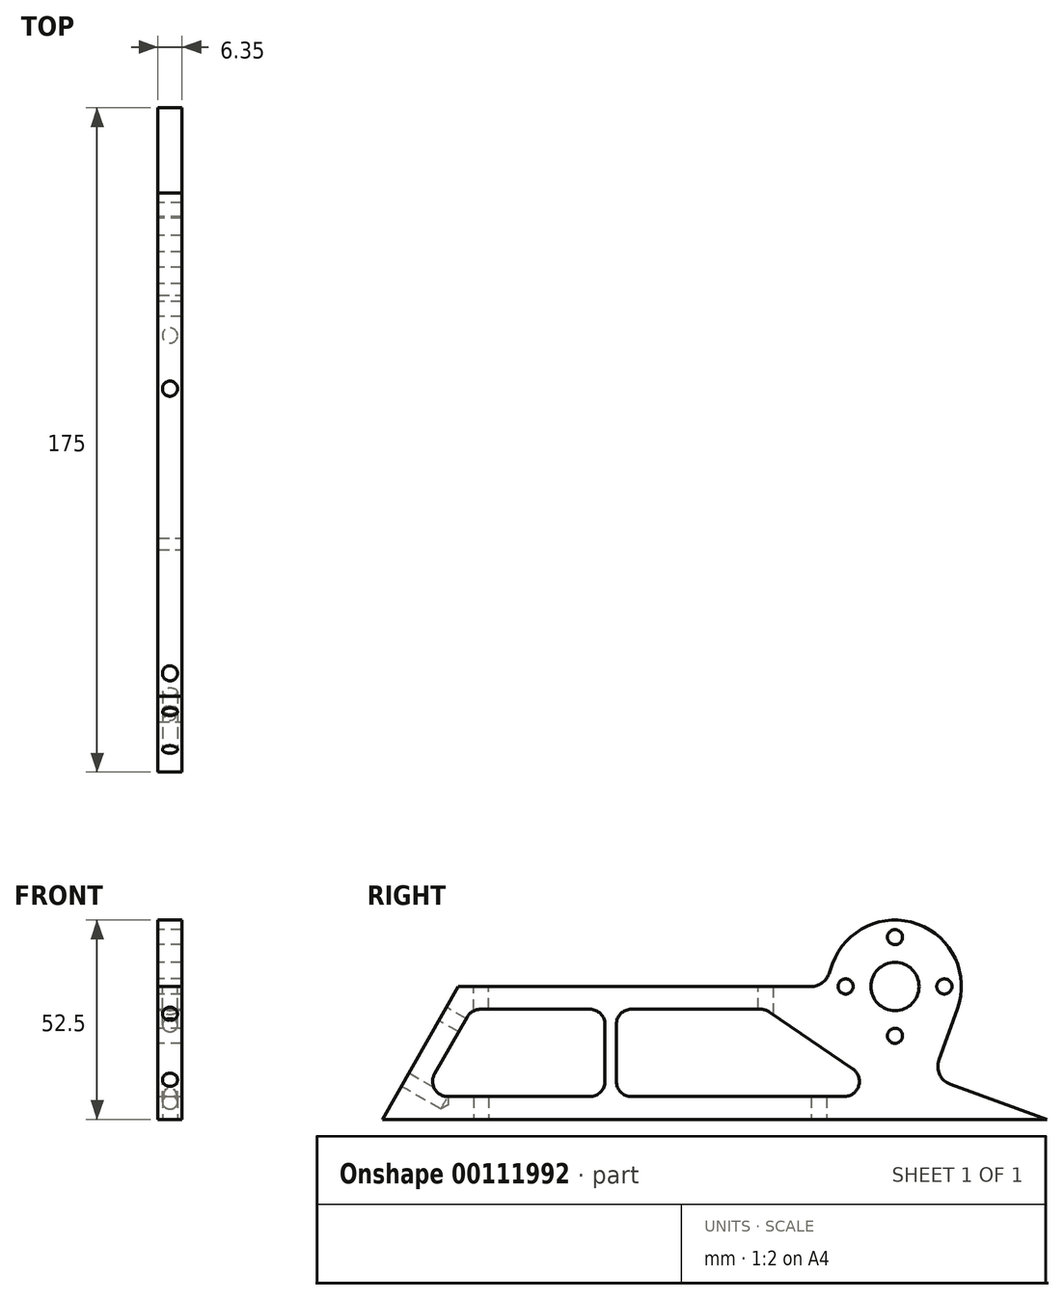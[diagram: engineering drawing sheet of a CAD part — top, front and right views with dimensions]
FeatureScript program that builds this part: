
annotation { "Feature Type Name" : "Feature", "Feature Type Description" : "" }
export const myFeature = defineFeature(function(context is Context, id is Id, definition is map)
    precondition{}
    {
        {
            var Q0;
            Q0=qCreatedBy(makeId("Right.planeOp"),FACE);
            var sketch = newSketch(context, id + "F0", { "sketchPlane" : qUnion([Q0])});
            skLineSegment(sketch, "E0", {"start": v(0, 0) * mm, "end": v(-30.13, 10.96) * mm});
            skLineSegment(sketch, "E1", {"start": v(-58.62, 35) * mm, "end": v(-155, 35) * mm});
            skLineSegment(sketch, "E2", {"start": v(-155, 35) * mm, "end": v(-175, 0) * mm});
            skLineSegment(sketch, "E3", {"start": v(-175, 0) * mm, "end": v(0, 0) * mm});
            skCircle(sketch, "E4", {"center": v(-88.38, 18) * mm, "radius": 14 * mm, "construction": true});
            skCircle(sketch, "E5", {"center": v(-40, 35) * mm, "radius": 34.3 * mm, "construction": true});
            skCircle(sketch, "E6", {"center": v(-130, 17.5) * mm, "radius": 11 * mm, "construction": true});
            skCircle(sketch, "E7", {"center": v(-40, 35) * mm, "radius": 6.35 * mm});
            skCircle(sketch, "E8", {"center": v(-40, 35) * mm, "radius": 13 * mm, "construction": true});
            skCircle(sketch, "E9", {"center": v(-40, 48) * mm, "radius": 2 * mm});
            skCircle(sketch, "E10", {"center": v(-53, 35) * mm, "radius": 2 * mm});
            skCircle(sketch, "E11", {"center": v(-27, 35) * mm, "radius": 2 * mm});
            skCircle(sketch, "E12", {"center": v(-40, 22) * mm, "radius": 2 * mm});
            skCircle(sketch, "E13", {"center": v(-130, 17.5) * mm, "radius": 25.4 * mm, "construction": true});
            skLineSegment(sketch, "E14", {"start": v(-130, 17.5) * mm, "end": v(-130, 35) * mm, "construction": true});
            skLineSegment(sketch, "E15", {"start": v(-130, 17.5) * mm, "end": v(-130, 0) * mm, "construction": true});
            skLineSegment(sketch, "E16", {"start": v(-58.62, 35) * mm, "end": v(-56.44, 40.99) * mm});
            skArc(sketch, "E17", {"start": v(-23.56, 29.01) * mm, "mid": v(-34.01, 51.44) * mm, "end": v(-56.44, 40.99) * mm});
            skLineSegment(sketch, "E18", {"start": v(-23.56, 29.01) * mm, "end": v(-30.13, 10.96) * mm});
            skPoint(sketch, "E19.orphan", {"position": v(-90, 35) * mm});
            skCircle(sketch, "E20", {"center": v(-130, 17.5) * mm, "radius": 2 * mm});
            skCircle(sketch, "E21", {"center": v(-88.38, 18) * mm, "radius": 3 * mm});
            skSolve(sketch);
        }
        {
            var Q0;
            Q0=qSketchRegion(id+"F0",true);
            extrude(context, id + "F1", {"entities" : qUnion([Q0]), "depth" : 6.35 * mm});
        }
        {
            var Q0;
            Q0=makeQuery(id+"F1.opExtrude","SWEPT_EDGE",EDGE,{"disambiguationData":[OSD([sQuery(id+"F0.wireOp",EDGE,"E1"),sQuery(id+"F0.wireOp",EDGE,"E16")])]});
            var Q1;
            Q1=makeQuery(id+"F1.opExtrude","SWEPT_EDGE",EDGE,{"disambiguationData":[OSD([sQuery(id+"F0.wireOp",EDGE,"E0"),sQuery(id+"F0.wireOp",EDGE,"E18")])]});
            fillet(context, id + "F2", {"entities" : qUnion([Q0, Q1]), "radius" : 5 * mm, "tangentPropagation" : true, "allowEdgeOverflow" : false});
        }
        {
            var Q0;
            Q0=makeQuery(id+"F1.opExtrude","CAP_FACE",FACE,{"disambiguationData":[OSD([sQuery(id+"F0.wireOp",EDGE,"E0"),sQuery(id+"F0.wireOp",EDGE,"E1"),sQuery(id+"F0.wireOp",EDGE,"E2"),sQuery(id+"F0.wireOp",EDGE,"E3"),sQuery(id+"F0.wireOp",EDGE,"E7"),sQuery(id+"F0.wireOp",EDGE,"E9"),sQuery(id+"F0.wireOp",EDGE,"E10"),sQuery(id+"F0.wireOp",EDGE,"E11"),sQuery(id+"F0.wireOp",EDGE,"E12"),sQuery(id+"F0.wireOp",EDGE,"E16"),sQuery(id+"F0.wireOp",EDGE,"E17"),sQuery(id+"F0.wireOp",EDGE,"E18"),sQuery(id+"F0.wireOp",EDGE,"E20"),sQuery(id+"F0.wireOp",EDGE,"E21")])],"isStart":false});
            var sketch = newSketch(context, id + "F3", { "sketchPlane" : qUnion([Q0])});
            skPoint(sketch, "E22", {"position": v(-130, 17.5) * mm});
            skLineSegment(sketch, "E23", {"start": v(-79.38, 25) * mm, "end": v(-79.38, 10) * mm});
            skLineSegment(sketch, "E24", {"start": v(-75.38, 6) * mm, "end": v(-53.38, 6) * mm});
            skLineSegment(sketch, "E25", {"start": v(-51.13, 13.3) * mm, "end": v(-73.13, 28.3) * mm});
            skPoint(sketch, "E26.visualSharp", {"position": v(-79.38, 32.57) * mm});
            skArc(sketch, "E26.filletArc", {"start": v(-73.13, 28.3) * mm, "mid": v(-77.25, 28.54) * mm, "end": v(-79.38, 25) * mm});
            skPoint(sketch, "E27.visualSharp", {"position": v(-40.41, 6) * mm});
            skArc(sketch, "E27.filletArc", {"start": v(-53.38, 6) * mm, "mid": v(-49.56, 8.82) * mm, "end": v(-51.13, 13.3) * mm});
            skPoint(sketch, "E28.visualSharp", {"position": v(-79.38, 6) * mm});
            skArc(sketch, "E28.filletArc", {"start": v(-79.38, 10) * mm, "mid": v(-78.2, 7.17) * mm, "end": v(-75.38, 6) * mm});
            skSolve(sketch);
        }
        {
            var Q0;
            Q0=qSketchRegion(id+"F3",true);
            extrude(context, id + "F4", {"entities" : qUnion([Q0]), "operationType" : NewBodyOperationType.REMOVE, "endBound" : BoundingType.THROUGH_ALL, "oppositeDirection" : true, "depth" : 25 * mm});
        }
        {
            var Q0;
            Q0=makeQuery(id+"F1.opExtrude","CAP_FACE",FACE,{"disambiguationData":[OSD([sQuery(id+"F0.wireOp",EDGE,"E0"),sQuery(id+"F0.wireOp",EDGE,"E1"),sQuery(id+"F0.wireOp",EDGE,"E2"),sQuery(id+"F0.wireOp",EDGE,"E3"),sQuery(id+"F0.wireOp",EDGE,"E7"),sQuery(id+"F0.wireOp",EDGE,"E9"),sQuery(id+"F0.wireOp",EDGE,"E10"),sQuery(id+"F0.wireOp",EDGE,"E11"),sQuery(id+"F0.wireOp",EDGE,"E12"),sQuery(id+"F0.wireOp",EDGE,"E16"),sQuery(id+"F0.wireOp",EDGE,"E17"),sQuery(id+"F0.wireOp",EDGE,"E18"),sQuery(id+"F0.wireOp",EDGE,"E20"),sQuery(id+"F0.wireOp",EDGE,"E21")])],"isStart":false});
            var sketch = newSketch(context, id + "F5", { "sketchPlane" : qUnion([Q0])});
            skLineSegment(sketch, "E29.bottom", {"start": v(-113.38, 29) * mm, "end": v(-75.38, 29) * mm});
            skLineSegment(sketch, "E29.top", {"start": v(-113.38, 6) * mm, "end": v(-75.38, 6) * mm});
            skLineSegment(sketch, "E29.left", {"start": v(-113.38, 29) * mm, "end": v(-113.38, 6) * mm});
            skLineSegment(sketch, "E29.right", {"start": v(-75.38, 29) * mm, "end": v(-75.38, 6) * mm});
            skLineSegment(sketch, "E30.bottom", {"start": v(-116.38, 29) * mm, "end": v(-151.52, 29) * mm});
            skLineSegment(sketch, "E30.top", {"start": v(-116.38, 6) * mm, "end": v(-164.66, 6) * mm});
            skLineSegment(sketch, "E30.left", {"start": v(-116.38, 29) * mm, "end": v(-116.38, 6) * mm});
            skLineSegment(sketch, "E30.right", {"start": v(-151.52, 29) * mm, "end": v(-164.66, 6) * mm});
            skPoint(sketch, "E31", {"position": v(-40, 35) * mm});
            skSolve(sketch);
        }
        {
            var Q0;
            Q0=qSketchRegion(id+"F5",true);
            extrude(context, id + "F6", {"entities" : qUnion([Q0]), "operationType" : NewBodyOperationType.REMOVE, "endBound" : BoundingType.THROUGH_ALL, "oppositeDirection" : true, "depth" : 25 * mm});
        }
        {
            var Q0;
            Q0=makeQuery(id+"F6.boolean.opBoolean","COPY",EDGE,{"derivedFrom":makeQuery(id+"F6.opExtrude","SWEPT_EDGE",EDGE,{"disambiguationData":[OSD([sQuery(id+"F5.wireOp",EDGE,"E30.bottom"),sQuery(id+"F5.wireOp",EDGE,"E30.left")])]})});
            var Q1;
            Q1=makeQuery(id+"F6.boolean.opBoolean","COPY",EDGE,{"derivedFrom":makeQuery(id+"F6.opExtrude","SWEPT_EDGE",EDGE,{"disambiguationData":[OSD([sQuery(id+"F5.wireOp",EDGE,"E29.bottom"),sQuery(id+"F5.wireOp",EDGE,"E29.right")])]})});
            var Q2;
            Q2=makeQuery(id+"F6.boolean.opBoolean","COPY",EDGE,{"derivedFrom":makeQuery(id+"F6.opExtrude","SWEPT_EDGE",EDGE,{"disambiguationData":[OSD([sQuery(id+"F5.wireOp",EDGE,"E30.top"),sQuery(id+"F5.wireOp",EDGE,"E30.left")])]})});
            var Q3;
            Q3=makeQuery(id+"F6.boolean.opBoolean","COPY",EDGE,{"derivedFrom":makeQuery(id+"F6.opExtrude","SWEPT_EDGE",EDGE,{"disambiguationData":[OSD([sQuery(id+"F5.wireOp",EDGE,"E29.top"),sQuery(id+"F5.wireOp",EDGE,"E29.right")])]})});
            var Q4;
            Q4=makeQuery(id+"F6.boolean.opBoolean","COPY",EDGE,{"derivedFrom":makeQuery(id+"F6.opExtrude","SWEPT_EDGE",EDGE,{"disambiguationData":[OSD([sQuery(id+"F5.wireOp",EDGE,"E29.top"),sQuery(id+"F5.wireOp",EDGE,"E29.left")])]})});
            var Q5;
            Q5=makeQuery(id+"F6.boolean.opBoolean","COPY",EDGE,{"derivedFrom":makeQuery(id+"F6.opExtrude","SWEPT_EDGE",EDGE,{"disambiguationData":[OSD([sQuery(id+"F5.wireOp",EDGE,"E30.top"),sQuery(id+"F5.wireOp",EDGE,"E30.right")])]})});
            var Q6;
            Q6=makeQuery(id+"F6.boolean.opBoolean","COPY",EDGE,{"derivedFrom":makeQuery(id+"F6.opExtrude","SWEPT_EDGE",EDGE,{"disambiguationData":[OSD([sQuery(id+"F5.wireOp",EDGE,"E30.bottom"),sQuery(id+"F5.wireOp",EDGE,"E30.right")])]})});
            var Q7;
            Q7=makeQuery(id+"F6.boolean.opBoolean","COPY",EDGE,{"derivedFrom":makeQuery(id+"F6.opExtrude","SWEPT_EDGE",EDGE,{"disambiguationData":[OSD([sQuery(id+"F5.wireOp",EDGE,"E29.bottom"),sQuery(id+"F5.wireOp",EDGE,"E29.left")])]})});
            fillet(context, id + "F7", {"entities" : qUnion([Q0, Q1, Q2, Q3, Q4, Q5, Q6, Q7]), "radius" : 4 * mm, "tangentPropagation" : true, "allowEdgeOverflow" : false});
        }
        {
            var Q0;
            Q0=makeQuery(id+"F1.opExtrude","SWEPT_FACE",FACE,{"disambiguationData":[OSD([sQuery(id+"F0.wireOp",EDGE,"E1")])]});
            var sketch = newSketch(context, id + "F8", { "sketchPlane" : qUnion([Q0])});
            skPoint(sketch, "E32", {"position": v(3.17, -74) * mm});
            skPoint(sketch, "E33", {"position": v(3.17, -149) * mm});
            skPoint(sketch, "E34", {"position": v(3.17, -155) * mm});
            skSolve(sketch);
        }
        {
            var Q0;
            Q0=sQuery(id+"F8.wireOp",VERTEX,"E32");
            var Q1;
            Q1=sQuery(id+"F8.wireOp",VERTEX,"E33");
            var Q2;
            Q2=makeQuery(id+"F1.opExtrude","SWEPT_BODY",BODY,{"disambiguationData":[OSD([sQuery(id+"F0.wireOp",EDGE,"E0"),sQuery(id+"F0.wireOp",EDGE,"E1"),sQuery(id+"F0.wireOp",EDGE,"E2"),sQuery(id+"F0.wireOp",EDGE,"E3"),sQuery(id+"F0.wireOp",EDGE,"E7"),sQuery(id+"F0.wireOp",EDGE,"E9"),sQuery(id+"F0.wireOp",EDGE,"E10"),sQuery(id+"F0.wireOp",EDGE,"E11"),sQuery(id+"F0.wireOp",EDGE,"E12"),sQuery(id+"F0.wireOp",EDGE,"E16"),sQuery(id+"F0.wireOp",EDGE,"E17"),sQuery(id+"F0.wireOp",EDGE,"E18"),sQuery(id+"F0.wireOp",EDGE,"E20"),sQuery(id+"F0.wireOp",EDGE,"E21")])]});
            hole(context, id + "F9", {"style" : HoleStyle.SIMPLE, "endStyle" : HoleEndStyle.BLIND, "holeDiameter" : 4 * mm, "holeDepth" : 12 * mm, "locations" : qUnion([Q0, Q1]), "scope" : qUnion([Q2])});
        }
        {
            var Q0;
            Q0=makeQuery(id+"F1.opExtrude","SWEPT_FACE",FACE,{"disambiguationData":[OSD([sQuery(id+"F0.wireOp",EDGE,"E2")])]});
            var sketch = newSketch(context, id + "F10", { "sketchPlane" : qUnion([Q0])});
            skPoint(sketch, "E35", {"position": v(3.17, -86.82) * mm});
            skPoint(sketch, "E36", {"position": v(3.17, -74.82) * mm});
            skPoint(sketch, "E37", {"position": v(3.17, -54.82) * mm});
            skSolve(sketch);
        }
        {
            var Q0;
            Q0=sQuery(id+"F10.wireOp",VERTEX,"E37");
            var Q1;
            Q1=sQuery(id+"F10.wireOp",VERTEX,"E36");
            var Q2;
            Q2=makeQuery(id+"F1.opExtrude","SWEPT_BODY",BODY,{"disambiguationData":[OSD([sQuery(id+"F0.wireOp",EDGE,"E0"),sQuery(id+"F0.wireOp",EDGE,"E1"),sQuery(id+"F0.wireOp",EDGE,"E2"),sQuery(id+"F0.wireOp",EDGE,"E3"),sQuery(id+"F0.wireOp",EDGE,"E7"),sQuery(id+"F0.wireOp",EDGE,"E9"),sQuery(id+"F0.wireOp",EDGE,"E10"),sQuery(id+"F0.wireOp",EDGE,"E11"),sQuery(id+"F0.wireOp",EDGE,"E12"),sQuery(id+"F0.wireOp",EDGE,"E16"),sQuery(id+"F0.wireOp",EDGE,"E17"),sQuery(id+"F0.wireOp",EDGE,"E18"),sQuery(id+"F0.wireOp",EDGE,"E20"),sQuery(id+"F0.wireOp",EDGE,"E21")])]});
            hole(context, id + "F11", {"style" : HoleStyle.SIMPLE, "endStyle" : HoleEndStyle.BLIND, "holeDiameter" : 4 * mm, "holeDepth" : 12 * mm, "locations" : qUnion([Q0, Q1]), "scope" : qUnion([Q2])});
        }
        {
            var Q0;
            Q0=makeQuery(id+"F1.opExtrude","SWEPT_FACE",FACE,{"disambiguationData":[OSD([sQuery(id+"F0.wireOp",EDGE,"E3")])]});
            var sketch = newSketch(context, id + "F12", { "sketchPlane" : qUnion([Q0])});
            skPoint(sketch, "E38", {"position": v(3.17, 175) * mm});
            skPoint(sketch, "E39", {"position": v(3.18, 149) * mm});
            skPoint(sketch, "E40", {"position": v(3.18, 60) * mm});
            skSolve(sketch);
        }
        {
            var Q0;
            Q0=sQuery(id+"F12.wireOp",VERTEX,"E39");
            var Q1;
            Q1=sQuery(id+"F12.wireOp",VERTEX,"E40");
            var Q2;
            Q2=makeQuery(id+"F1.opExtrude","SWEPT_BODY",BODY,{"disambiguationData":[OSD([sQuery(id+"F0.wireOp",EDGE,"E0"),sQuery(id+"F0.wireOp",EDGE,"E1"),sQuery(id+"F0.wireOp",EDGE,"E2"),sQuery(id+"F0.wireOp",EDGE,"E3"),sQuery(id+"F0.wireOp",EDGE,"E7"),sQuery(id+"F0.wireOp",EDGE,"E9"),sQuery(id+"F0.wireOp",EDGE,"E10"),sQuery(id+"F0.wireOp",EDGE,"E11"),sQuery(id+"F0.wireOp",EDGE,"E12"),sQuery(id+"F0.wireOp",EDGE,"E16"),sQuery(id+"F0.wireOp",EDGE,"E17"),sQuery(id+"F0.wireOp",EDGE,"E18"),sQuery(id+"F0.wireOp",EDGE,"E20"),sQuery(id+"F0.wireOp",EDGE,"E21")])]});
            hole(context, id + "F13", {"style" : HoleStyle.SIMPLE, "endStyle" : HoleEndStyle.BLIND, "holeDiameter" : 4 * mm, "holeDepth" : 12 * mm, "locations" : qUnion([Q0, Q1]), "scope" : qUnion([Q2])});
        }
    });
